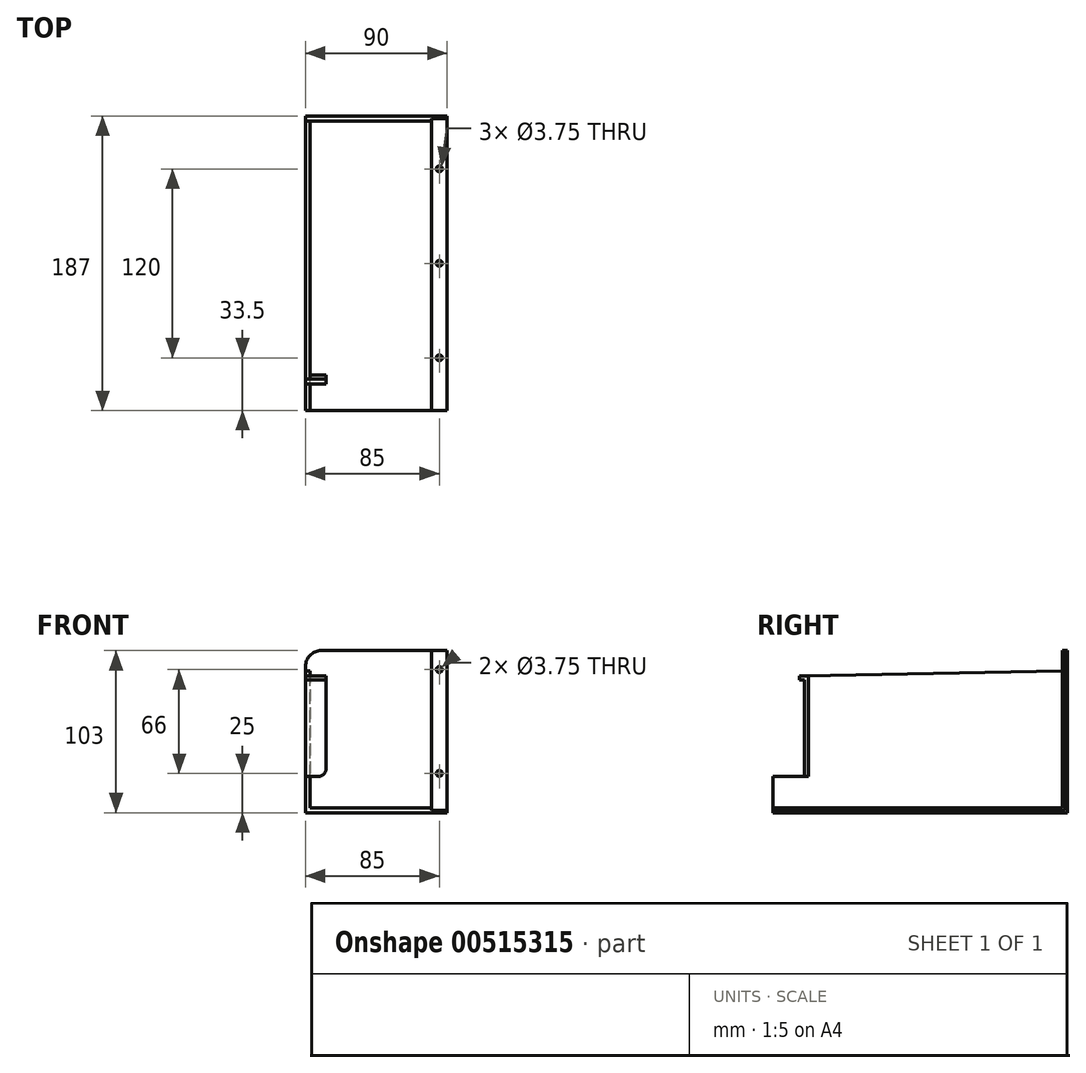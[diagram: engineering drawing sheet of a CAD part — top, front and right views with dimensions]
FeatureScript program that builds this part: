
annotation { "Feature Type Name" : "Feature", "Feature Type Description" : "" }
export const myFeature = defineFeature(function(context is Context, id is Id, definition is map)
    precondition{}
    {
        {
            var Q0;
            Q0=qCreatedBy(makeId("Top.planeOp"),FACE);
            var sketch = newSketch(context, id + "F0", { "sketchPlane" : qUnion([Q0])});
            skLineSegment(sketch, "E0.bottom", {"start": v(0, 93.5) * mm, "end": v(-80, 93.5) * mm});
            skLineSegment(sketch, "E0.top", {"start": v(0, -93.5) * mm, "end": v(-80, -93.5) * mm});
            skLineSegment(sketch, "E0.left", {"start": v(0, 93.5) * mm, "end": v(0, -93.5) * mm});
            skLineSegment(sketch, "E0.right", {"start": v(-80, 93.5) * mm, "end": v(-80, -93.5) * mm});
            skSolve(sketch);
        }
        {
            var Q0;
            Q0 = qSketchRegion(id + "F0", true);
            extrude(context, id + "F1", {"entities" : qUnion([Q0]), "depth" : 3 * mm, "offsetDistance" : 25 * mm});
        }
        {
            var Q0;
            Q0=makeQuery(id+"F1.opExtrude","CAP_FACE",FACE,{"disambiguationData":[OSD([sQuery(id+"F0.wireOp",EDGE,"E0.bottom"),sQuery(id+"F0.wireOp",EDGE,"E0.top"),sQuery(id+"F0.wireOp",EDGE,"E0.left"),sQuery(id+"F0.wireOp",EDGE,"E0.right")])],"isStart":false});
            var sketch = newSketch(context, id + "F2", { "sketchPlane" : qUnion([Q0])});
            skLineSegment(sketch, "E1.bottom", {"start": v(-80, 93.5) * mm, "end": v(0, 93.5) * mm});
            skLineSegment(sketch, "E1.top", {"start": v(-80, 90.5) * mm, "end": v(0, 90.5) * mm});
            skLineSegment(sketch, "E1.left", {"start": v(-80, 93.5) * mm, "end": v(-80, 90.5) * mm});
            skLineSegment(sketch, "E1.right", {"start": v(0, 93.5) * mm, "end": v(0, 90.5) * mm});
            skSolve(sketch);
        }
        {
            var Q0;
            Q0 = qSketchRegion(id + "F2", true);
            extrude(context, id + "F3", {"entities" : qUnion([Q0]), "operationType" : NewBodyOperationType.ADD, "depth" : 100 * mm, "offsetDistance" : 25 * mm});
        }
        {
            var Q0;
            Q0=makeQuery(id+"F3.boolean.opBoolean","MERGE",FACE,{"derivedFrom":[makeQuery(id+"F1.opExtrude","SWEPT_FACE",FACE,{"disambiguationData":[OSD([sQuery(id+"F0.wireOp",EDGE,"E0.right")])]}),makeQuery(id+"F3.opExtrude","SWEPT_FACE",FACE,{"disambiguationData":[OSD([sQuery(id+"F2.wireOp",EDGE,"E1.left")])]})]});
            var sketch = newSketch(context, id + "F4", { "sketchPlane" : qUnion([Q0])});
            skLineSegment(sketch, "E2", {"start": v(-90.5, 3) * mm, "end": v(-90.5, 90) * mm});
            skLineSegment(sketch, "E3", {"start": v(-90.5, 90) * mm, "end": v(73.5, 87) * mm});
            skLineSegment(sketch, "E4", {"start": v(73.5, 87) * mm, "end": v(73.5, 23) * mm});
            skLineSegment(sketch, "E5", {"start": v(93.5, 3) * mm, "end": v(-90.5, 3) * mm});
            skLineSegment(sketch, "E6", {"start": v(93.5, 3) * mm, "end": v(93.5, 23) * mm});
            skLineSegment(sketch, "E7", {"start": v(93.5, 23) * mm, "end": v(73.5, 23) * mm});
            skLineSegment(sketch, "E8", {"start": v(73.5, 23) * mm, "end": v(73.5, 23) * mm});
            skSolve(sketch);
        }
        {
            var Q0;
            Q0 = qSketchRegion(id + "F4", true);
            extrude(context, id + "F5", {"entities" : qUnion([Q0]), "operationType" : NewBodyOperationType.ADD, "oppositeDirection" : true, "depth" : 3 * mm, "offsetDistance" : 25 * mm});
        }
        {
            var Q0;
            Q0=makeQuery(id+"F5.opExtrude","CAP_FACE",FACE,{"disambiguationData":[OSD([sQuery(id+"F4.wireOp",EDGE,"E2"),sQuery(id+"F4.wireOp",EDGE,"E3"),sQuery(id+"F4.wireOp",EDGE,"E4"),sQuery(id+"F4.wireOp",EDGE,"E5"),sQuery(id+"F4.wireOp",EDGE,"E6"),sQuery(id+"F4.wireOp",EDGE,"E7")])],"isStart":false});
            var sketch = newSketch(context, id + "F6", { "sketchPlane" : qUnion([Q0])});
            skLineSegment(sketch, "E9", {"start": v(-73.5, 87) * mm, "end": v(-73.5, 23) * mm});
            skLineSegment(sketch, "E10", {"start": v(-73.5, 23) * mm, "end": v(-71, 23) * mm});
            skLineSegment(sketch, "E11", {"start": v(-71, 23) * mm, "end": v(-71, 86.54) * mm});
            skLineSegment(sketch, "E12", {"start": v(-73.5, 87) * mm, "end": v(-71, 86.54) * mm});
            skSolve(sketch);
        }
        {
            var Q0;
            Q0 = qSketchRegion(id + "F6", true);
            extrude(context, id + "F7", {"entities" : qUnion([Q0]), "operationType" : NewBodyOperationType.ADD, "depth" : 10 * mm, "offsetDistance" : 25 * mm});
        }
        {
            var Q0;
            Q0=makeQuery(id+"F7.boolean.opBoolean","MERGE",FACE,{"derivedFrom":[makeQuery(id+"F5.opExtrude","SWEPT_FACE",FACE,{"disambiguationData":[OSD([sQuery(id+"F4.wireOp",EDGE,"E4")])]}),makeQuery(id+"F7.opExtrude","SWEPT_FACE",FACE,{"disambiguationData":[OSD([sQuery(id+"F6.wireOp",EDGE,"E9")])]})]});
            var sketch = newSketch(context, id + "F8", { "sketchPlane" : qUnion([Q0])});
            skLineSegment(sketch, "E13.bottom", {"start": v(-67, 87) * mm, "end": v(-80, 87) * mm});
            skLineSegment(sketch, "E13.top", {"start": v(-67, 84.5) * mm, "end": v(-80, 84.5) * mm});
            skLineSegment(sketch, "E13.left", {"start": v(-67, 87) * mm, "end": v(-67, 84.5) * mm});
            skLineSegment(sketch, "E13.right", {"start": v(-80, 87) * mm, "end": v(-80, 84.5) * mm});
            skSolve(sketch);
        }
        {
            var Q0;
            Q0 = qSketchRegion(id + "F8", true);
            extrude(context, id + "F9", {"entities" : qUnion([Q0]), "operationType" : NewBodyOperationType.ADD, "depth" : 3 * mm, "offsetDistance" : 25 * mm});
        }
        {
            var Q0;
            Q0=makeQuery(id+"F3.opExtrude","CAP_EDGE",EDGE,{"disambiguationData":[OSD([sQuery(id+"F2.wireOp",EDGE,"E1.left")])],"isStart":false});
            fillet(context, id + "F10", {"entities" : qUnion([Q0]), "radius" : 10 * mm, "tangentPropagation" : true, "allowEdgeOverflow" : false});
        }
        {
            var Q0;
            Q0=makeQuery(id+"F7.opExtrude","CAP_EDGE",EDGE,{"disambiguationData":[OSD([sQuery(id+"F6.wireOp",EDGE,"E10")])],"isStart":false});
            fillet(context, id + "F11", {"entities" : qUnion([Q0]), "radius" : 5 * mm, "tangentPropagation" : true, "allowEdgeOverflow" : false});
        }
        {
            var Q0;
            Q0=makeQuery(id+"F3.boolean.opBoolean","MERGE",FACE,{"derivedFrom":[makeQuery(id+"F1.opExtrude","SWEPT_FACE",FACE,{"disambiguationData":[OSD([sQuery(id+"F0.wireOp",EDGE,"E0.left")])]}),makeQuery(id+"F3.opExtrude","SWEPT_FACE",FACE,{"disambiguationData":[OSD([sQuery(id+"F2.wireOp",EDGE,"E1.right")])]})]});
            var sketch = newSketch(context, id + "F12", { "sketchPlane" : qUnion([Q0])});
            skLineSegment(sketch, "E14", {"start": v(93.5, 103) * mm, "end": v(93.5, 0) * mm});
            skLineSegment(sketch, "E15", {"start": v(93.5, 0) * mm, "end": v(-93.5, 0) * mm});
            skLineSegment(sketch, "E16", {"start": v(-93.5, 0) * mm, "end": v(-93.5, 1.5) * mm});
            skLineSegment(sketch, "E17", {"start": v(-93.5, 1.5) * mm, "end": v(92, 1.5) * mm});
            skLineSegment(sketch, "E18", {"start": v(92, 1.5) * mm, "end": v(92, 103) * mm});
            skLineSegment(sketch, "E19", {"start": v(92, 103) * mm, "end": v(93.5, 103) * mm});
            skSolve(sketch);
        }
        {
            var Q0;
            Q0 = qSketchRegion(id + "F12", true);
            extrude(context, id + "F13", {"entities" : qUnion([Q0]), "operationType" : NewBodyOperationType.ADD, "depth" : 10 * mm, "offsetDistance" : 25 * mm});
        }
        {
            var Q0;
            Q0=makeQuery(id+"F13.opExtrude","SWEPT_FACE",FACE,{"disambiguationData":[OSD([sQuery(id+"F12.wireOp",EDGE,"E17")])]});
            var sketch = newSketch(context, id + "F14", { "sketchPlane" : qUnion([Q0])});
            skPoint(sketch, "E20", {"position": v(5, 60) * mm});
            skPoint(sketch, "E21", {"position": v(5, -60) * mm});
            skPoint(sketch, "E22", {"position": v(5, 0) * mm});
            skSolve(sketch);
        }
        {
            var Q0;
            Q0=makeQuery(id+"F13.opExtrude","SWEPT_FACE",FACE,{"disambiguationData":[OSD([sQuery(id+"F12.wireOp",EDGE,"E18")])]});
            var sketch = newSketch(context, id + "F15", { "sketchPlane" : qUnion([Q0])});
            skPoint(sketch, "E23", {"position": v(5, 91) * mm});
            skPoint(sketch, "E24", {"position": v(5, 25) * mm});
            skSolve(sketch);
        }
        {
            var Q0;
            Q0=sQuery(id+"F14.wireOp",VERTEX,"E21");
            var Q1;
            Q1=sQuery(id+"F14.wireOp",VERTEX,"E22");
            var Q2;
            Q2=sQuery(id+"F14.wireOp",VERTEX,"E20");
            var Q3;
            Q3=sQuery(id+"F15.wireOp",VERTEX,"E24");
            var Q4;
            Q4=sQuery(id+"F15.wireOp",VERTEX,"E23");
            var Q5;
            Q5=makeQuery(id+"F1.opExtrude","SWEPT_BODY",BODY,{"disambiguationData":[OSD([sQuery(id+"F0.wireOp",EDGE,"E0.bottom"),sQuery(id+"F0.wireOp",EDGE,"E0.top"),sQuery(id+"F0.wireOp",EDGE,"E0.left"),sQuery(id+"F0.wireOp",EDGE,"E0.right")])]});
            hole(context, id + "F16", {"style" : HoleStyle.SIMPLE, "endStyle" : HoleEndStyle.BLIND, "holeDiameter" : 3.75 * mm, "majorDiameter" : 5 * mm, "holeDepth" : 4.5 * mm, "isTappedThrough" : true, "tappedDepth" : 12 * mm, "tapClearance" : 3, "locations" : qUnion([Q0, Q1, Q2, Q3, Q4]), "scope" : qUnion([Q5]), "startStyle" : HoleStartStyle.SKETCH});
        }
    });
